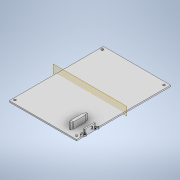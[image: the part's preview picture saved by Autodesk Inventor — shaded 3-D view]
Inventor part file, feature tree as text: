
AUTODESK INVENTOR PART (.ipt)
format: ipt  version: 2020.1 (Build 241239000, 239)  size: 183,808 bytes
history: native  units: mm
features: sketch x7, extrude x4, hole x2, plane x1, mirror x1
ambient origin geometry x8: Origin, YZ Plane, XZ Plane, XY Plane, X Axis, Y Axis, Z Axis, Center Point
bodies: Solid1 (feature_tree)
feature tree (15):
  extrude  "Extrusion1"  Depth=120.0mm
  extrude  "Extrusion2"  Depth=2.4mm
  extrude  "Extrusion3"  Depth=15.25mm
  extrude  "Extrusion4"  Depth=1.25mm
  plane  "Work Plane3"
  hole  "Hole1"  [1 undecoded]
  sketch  "Sketch12"  dims[d12=2.5mm d13=8.25mm d14=0.0mm]
  hole  "Hole2"  [1 undecoded]
  mirror  "Mirror4"
  sketch  "Sketch1"  dims[d0=168.0mm d1=120.0mm]
  sketch  "Sketch2"  dims[d2=2.4mm d3=0.0mm d4=2.4mm]
  sketch  "Sketch3"  dims[d5=17.5mm d6=15.25mm]
  sketch  "Sketch4"  dims[d7=8.25mm d8=0.0mm d9=1.25mm]
  sketch  "Sketch11"  dims[d10=2.5mm d11=1.25mm]
  sketch  "Sketch13"  dims[d15=18.5mm d16=13.0mm d17=5.0mm d18=22.0mm d19=11.25mm d20=0.0mm d21=2.625mm d22=8.0mm d23=2.625mm d24=8.0mm d63=6.0mm d64=4.0mm d65=4.0mm d66=6.0mm d67=4.0mm d68=6.0mm d69=8.4mm d70=2.0mm d71=90.0deg d72=8.0mm d73=20.594885mm d74=6.0mm d75=6.0mm d76=4.0mm d77=6.0mm d78=8.4mm d79=2.0mm d80=90.0deg d81=10.0mm d82=20.594885mm]
note: 2 required parameter values undecoded (feature->parameter linkage not recoverable at this tier; creation-order binding heuristic only, values carry confidence <= 0.55)
